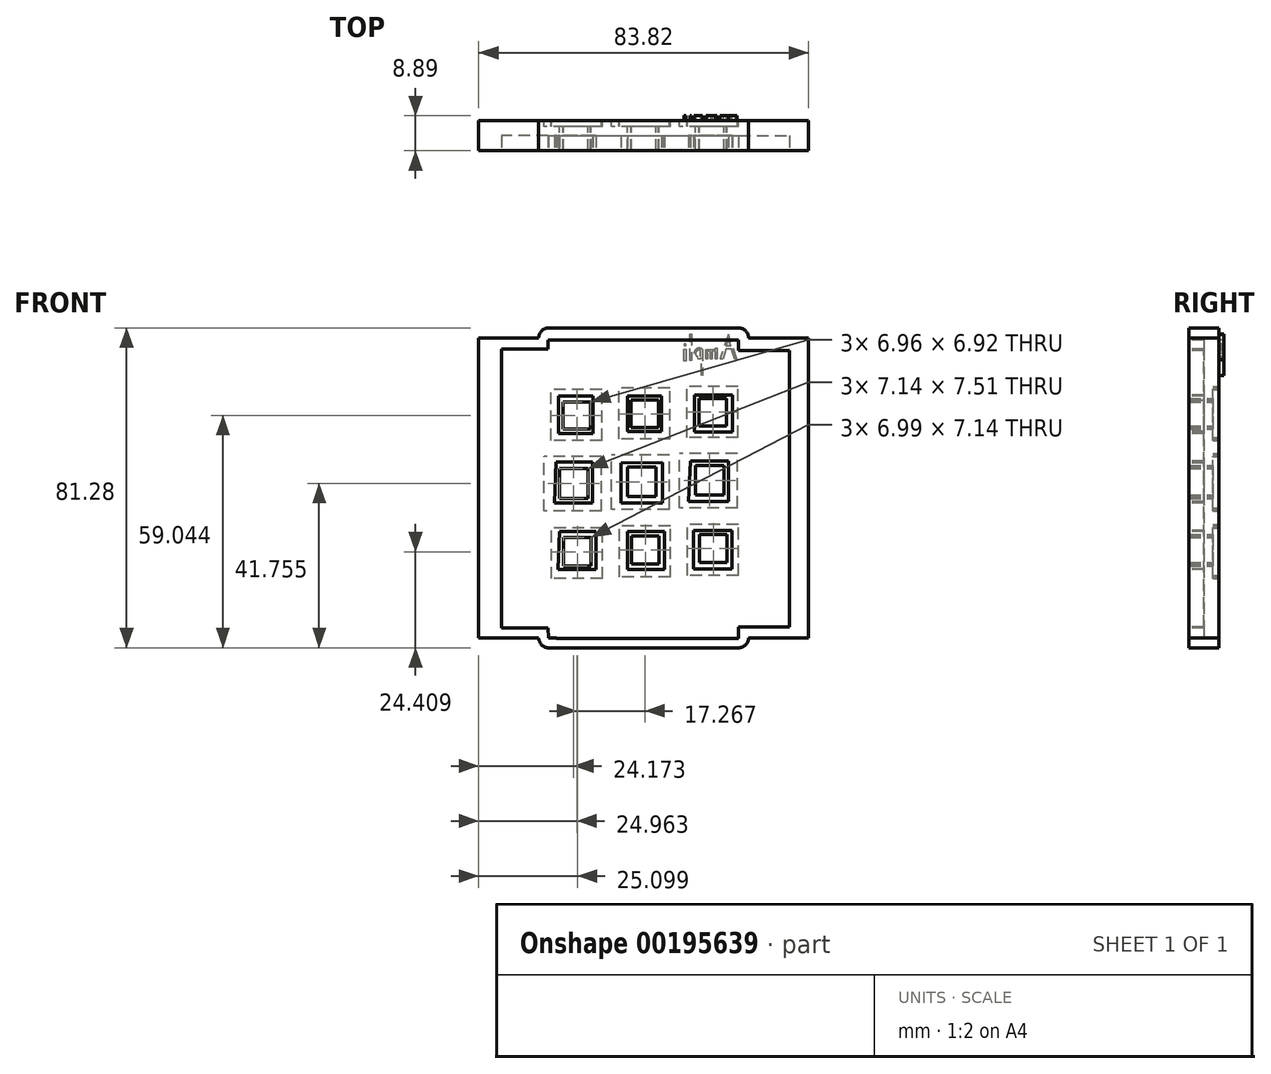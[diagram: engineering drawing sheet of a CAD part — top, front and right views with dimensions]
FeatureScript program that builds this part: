
annotation { "Feature Type Name" : "Feature", "Feature Type Description" : "" }
export const myFeature = defineFeature(function(context is Context, id is Id, definition is map)
    precondition{}
    {
        {
            var Q0;
            Q0=qCreatedBy(makeId("Front.planeOp"),FACE);
            var sketch = newSketch(context, id + "F0", { "sketchPlane" : qUnion([Q0])});
            skLineSegment(sketch, "E0.bottom", {"start": v(26.67, 27.94) * mm, "end": v(-26.67, 27.94) * mm});
            skLineSegment(sketch, "E0.top", {"start": v(26.67, -27.94) * mm, "end": v(-26.67, -27.94) * mm});
            skLineSegment(sketch, "E0.left", {"start": v(26.67, 27.94) * mm, "end": v(26.67, -27.94) * mm});
            skLineSegment(sketch, "E0.right", {"start": v(-26.67, 27.94) * mm, "end": v(-26.67, -27.94) * mm});
            skPoint(sketch, "E0.middle", {"position": v(0, 0) * mm});
            skSolve(sketch);
        }
        {
            var Q0;
            Q0 = qSketchRegion(id + "F0", true);
            extrude(context, id + "F1", {"entities" : qUnion([Q0]), "depth" : 7.62 * mm});
        }
        {
            var Q0;
            Q0=makeQuery(id+"F1.opExtrude","CAP_FACE",FACE,{"disambiguationData":[OSD([sQuery(id+"F0.wireOp",EDGE,"E0.bottom"),sQuery(id+"F0.wireOp",EDGE,"E0.top"),sQuery(id+"F0.wireOp",EDGE,"E0.left"),sQuery(id+"F0.wireOp",EDGE,"E0.right")])],"isStart":true});
            var sketch = newSketch(context, id + "F2", { "sketchPlane" : qUnion([Q0])});
            skLineSegment(sketch, "E1.bottom", {"start": v(-21.07, 22.68) * mm, "end": v(-14.1, 22.68) * mm});
            skLineSegment(sketch, "E1.top", {"start": v(-21.07, 15.76) * mm, "end": v(-14.1, 15.76) * mm});
            skLineSegment(sketch, "E1.left", {"start": v(-21.07, 22.68) * mm, "end": v(-21.07, 15.76) * mm});
            skLineSegment(sketch, "E1.right", {"start": v(-14.1, 22.68) * mm, "end": v(-14.1, 15.76) * mm});
            skLineSegment(sketch, "E2.bottom", {"start": v(-23.93, 12.85) * mm, "end": v(-11, 12.85) * mm});
            skLineSegment(sketch, "E2.top", {"start": v(-23.93, 25.79) * mm, "end": v(-11, 25.79) * mm});
            skLineSegment(sketch, "E2.left", {"start": v(-23.93, 12.85) * mm, "end": v(-23.93, 25.79) * mm});
            skLineSegment(sketch, "E2.right", {"start": v(-11, 12.85) * mm, "end": v(-11, 25.79) * mm});
            skLineSegment(sketch, "E3.1.0.0", {"start": v(3.16, 22.27) * mm, "end": v(3.16, 15.35) * mm});
            skLineSegment(sketch, "E3.1.0.1", {"start": v(-3.8, 15.35) * mm, "end": v(3.16, 15.35) * mm});
            skLineSegment(sketch, "E3.1.0.2", {"start": v(-3.8, 22.27) * mm, "end": v(-3.8, 15.35) * mm});
            skLineSegment(sketch, "E3.1.0.3", {"start": v(-3.8, 22.27) * mm, "end": v(3.16, 22.27) * mm});
            skLineSegment(sketch, "E3.1.0.4", {"start": v(6.27, 12.45) * mm, "end": v(6.27, 25.38) * mm});
            skLineSegment(sketch, "E3.1.0.5", {"start": v(-6.66, 12.45) * mm, "end": v(-6.66, 25.38) * mm});
            skLineSegment(sketch, "E3.1.0.6", {"start": v(-6.66, 12.45) * mm, "end": v(6.27, 12.45) * mm});
            skLineSegment(sketch, "E3.1.0.7", {"start": v(-6.66, 25.38) * mm, "end": v(6.27, 25.38) * mm});
            skLineSegment(sketch, "E3.2.0.0", {"start": v(20.43, 21.86) * mm, "end": v(20.43, 14.95) * mm});
            skLineSegment(sketch, "E3.2.0.1", {"start": v(13.46, 14.95) * mm, "end": v(20.43, 14.95) * mm});
            skLineSegment(sketch, "E3.2.0.2", {"start": v(13.46, 21.86) * mm, "end": v(13.46, 14.95) * mm});
            skLineSegment(sketch, "E3.2.0.3", {"start": v(13.46, 21.86) * mm, "end": v(20.43, 21.86) * mm});
            skLineSegment(sketch, "E3.2.0.4", {"start": v(23.54, 12.04) * mm, "end": v(23.54, 24.97) * mm});
            skLineSegment(sketch, "E3.2.0.5", {"start": v(10.6, 12.04) * mm, "end": v(10.6, 24.97) * mm});
            skLineSegment(sketch, "E3.2.0.6", {"start": v(10.6, 12.04) * mm, "end": v(23.54, 12.04) * mm});
            skLineSegment(sketch, "E3.2.0.7", {"start": v(10.6, 24.97) * mm, "end": v(23.54, 24.97) * mm});
            skLineSegment(sketch, "E3.direction1", {"start": v(-23.93, 12.85) * mm, "end": v(-6.66, 12.45) * mm, "construction": true});
            skPoint(sketch, "E4", {"position": v(0, 0) * mm});
            skPoint(sketch, "E5", {"position": v(-0.84, 0.87) * mm});
            skPoint(sketch, "E6", {"position": v(-0.84, -16.23) * mm});
            skLineSegment(sketch, "E7.bottom", {"start": v(-20.37, 5.69) * mm, "end": v(-13.23, 5.69) * mm});
            skLineSegment(sketch, "E7.top", {"start": v(-20.37, -1.83) * mm, "end": v(-13.23, -1.83) * mm});
            skLineSegment(sketch, "E7.left", {"start": v(-20.37, 5.69) * mm, "end": v(-20.37, -1.83) * mm});
            skLineSegment(sketch, "E7.right", {"start": v(-13.23, 5.69) * mm, "end": v(-13.23, -1.83) * mm});
            skLineSegment(sketch, "E8.bottom", {"start": v(-23.8, -5.1) * mm, "end": v(-9.18, -5.1) * mm});
            skLineSegment(sketch, "E8.top", {"start": v(-23.8, 8.75) * mm, "end": v(-9.18, 8.75) * mm});
            skLineSegment(sketch, "E8.left", {"start": v(-23.8, -5.1) * mm, "end": v(-23.8, 8.75) * mm});
            skLineSegment(sketch, "E8.right", {"start": v(-9.18, -5.1) * mm, "end": v(-9.18, 8.75) * mm});
            skLineSegment(sketch, "E9.1.0.0", {"start": v(4.04, 5.28) * mm, "end": v(4.04, -2.23) * mm});
            skLineSegment(sketch, "E9.1.0.1", {"start": v(-3.1, -2.23) * mm, "end": v(4.04, -2.23) * mm});
            skLineSegment(sketch, "E9.1.0.2", {"start": v(-3.1, 5.28) * mm, "end": v(-3.1, -2.23) * mm});
            skLineSegment(sketch, "E9.1.0.3", {"start": v(-3.1, 5.28) * mm, "end": v(4.04, 5.28) * mm});
            skLineSegment(sketch, "E9.1.0.4", {"start": v(8.09, -5.5) * mm, "end": v(8.09, 8.34) * mm});
            skLineSegment(sketch, "E9.1.0.5", {"start": v(-6.54, -5.5) * mm, "end": v(-6.54, 8.34) * mm});
            skLineSegment(sketch, "E9.1.0.6", {"start": v(-6.54, -5.5) * mm, "end": v(8.09, -5.5) * mm});
            skLineSegment(sketch, "E9.1.0.7", {"start": v(-6.54, 8.34) * mm, "end": v(8.09, 8.34) * mm});
            skLineSegment(sketch, "E9.2.0.0", {"start": v(21.3, 4.87) * mm, "end": v(21.3, -2.64) * mm});
            skLineSegment(sketch, "E9.2.0.1", {"start": v(14.17, -2.64) * mm, "end": v(21.3, -2.64) * mm});
            skLineSegment(sketch, "E9.2.0.2", {"start": v(14.17, 4.87) * mm, "end": v(14.17, -2.64) * mm});
            skLineSegment(sketch, "E9.2.0.3", {"start": v(14.17, 4.87) * mm, "end": v(21.3, 4.87) * mm});
            skLineSegment(sketch, "E9.2.0.4", {"start": v(25.36, -5.91) * mm, "end": v(25.36, 7.93) * mm});
            skLineSegment(sketch, "E9.2.0.5", {"start": v(10.73, -5.91) * mm, "end": v(10.73, 7.93) * mm});
            skLineSegment(sketch, "E9.2.0.6", {"start": v(10.73, -5.91) * mm, "end": v(25.36, -5.91) * mm});
            skLineSegment(sketch, "E9.2.0.7", {"start": v(10.73, 7.93) * mm, "end": v(25.36, 7.93) * mm});
            skLineSegment(sketch, "E9.direction1", {"start": v(-23.8, -5.1) * mm, "end": v(-6.54, -5.5) * mm, "construction": true});
            skLineSegment(sketch, "E10.bottom", {"start": v(-21.22, -11.85) * mm, "end": v(-14.23, -11.85) * mm});
            skLineSegment(sketch, "E10.top", {"start": v(-21.22, -18.99) * mm, "end": v(-14.23, -18.99) * mm});
            skLineSegment(sketch, "E10.left", {"start": v(-21.22, -11.85) * mm, "end": v(-21.22, -18.99) * mm});
            skLineSegment(sketch, "E10.right", {"start": v(-14.23, -11.85) * mm, "end": v(-14.23, -18.99) * mm});
            skLineSegment(sketch, "E11.bottom", {"start": v(-24.05, -22.26) * mm, "end": v(-11.12, -22.26) * mm});
            skLineSegment(sketch, "E11.top", {"start": v(-24.05, -9.33) * mm, "end": v(-11.12, -9.33) * mm});
            skLineSegment(sketch, "E11.left", {"start": v(-24.05, -22.26) * mm, "end": v(-24.05, -9.33) * mm});
            skLineSegment(sketch, "E11.right", {"start": v(-11.12, -22.26) * mm, "end": v(-11.12, -9.33) * mm});
            skLineSegment(sketch, "E12.1.0.0", {"start": v(3.04, -12.25) * mm, "end": v(3.04, -19.4) * mm});
            skLineSegment(sketch, "E12.1.0.1", {"start": v(-3.95, -19.4) * mm, "end": v(3.04, -19.4) * mm});
            skLineSegment(sketch, "E12.1.0.2", {"start": v(-3.95, -12.25) * mm, "end": v(-3.95, -19.4) * mm});
            skLineSegment(sketch, "E12.1.0.3", {"start": v(-3.95, -12.25) * mm, "end": v(3.04, -12.25) * mm});
            skLineSegment(sketch, "E12.1.0.4", {"start": v(6.15, -22.67) * mm, "end": v(6.15, -9.74) * mm});
            skLineSegment(sketch, "E12.1.0.5", {"start": v(-6.78, -22.67) * mm, "end": v(-6.78, -9.74) * mm});
            skLineSegment(sketch, "E12.1.0.6", {"start": v(-6.78, -22.67) * mm, "end": v(6.15, -22.67) * mm});
            skLineSegment(sketch, "E12.1.0.7", {"start": v(-6.78, -9.74) * mm, "end": v(6.15, -9.74) * mm});
            skLineSegment(sketch, "E12.2.0.0", {"start": v(20.3, -12.66) * mm, "end": v(20.3, -19.8) * mm});
            skLineSegment(sketch, "E12.2.0.1", {"start": v(13.32, -19.8) * mm, "end": v(20.3, -19.8) * mm});
            skLineSegment(sketch, "E12.2.0.2", {"start": v(13.32, -12.66) * mm, "end": v(13.32, -19.8) * mm});
            skLineSegment(sketch, "E12.2.0.3", {"start": v(13.32, -12.66) * mm, "end": v(20.3, -12.66) * mm});
            skLineSegment(sketch, "E12.2.0.4", {"start": v(23.42, -23.08) * mm, "end": v(23.42, -10.14) * mm});
            skLineSegment(sketch, "E12.2.0.5", {"start": v(10.48, -23.08) * mm, "end": v(10.48, -10.14) * mm});
            skLineSegment(sketch, "E12.2.0.6", {"start": v(10.48, -23.08) * mm, "end": v(23.42, -23.08) * mm});
            skLineSegment(sketch, "E12.2.0.7", {"start": v(10.48, -10.14) * mm, "end": v(23.42, -10.14) * mm});
            skLineSegment(sketch, "E12.direction1", {"start": v(-24.05, -22.26) * mm, "end": v(-6.78, -22.67) * mm, "construction": true});
            skSolve(sketch);
        }
        {
            var Q0;
            Q0=makeQuery(id+"F2.imprint","IMPRINT",FACE,{"disambiguationData":[TD([[makeQuery(id+"F2.imprint","IMPRINT",EDGE,{"derivedFrom":sQuery(id+"F2.wireOp",EDGE,"E1.bottom")}),-1.0]])]});
            var Q1;
            Q1=makeQuery(id+"F2.imprint","IMPRINT",FACE,{"disambiguationData":[TD([[makeQuery(id+"F2.imprint","IMPRINT",EDGE,{"derivedFrom":sQuery(id+"F2.wireOp",EDGE,"E3.1.0.0")}),-1.0]])]});
            var Q2;
            Q2=makeQuery(id+"F2.imprint","IMPRINT",FACE,{"disambiguationData":[TD([[makeQuery(id+"F2.imprint","IMPRINT",EDGE,{"derivedFrom":sQuery(id+"F2.wireOp",EDGE,"E9.2.0.0")}),-1.0]])]});
            var Q3;
            Q3=makeQuery(id+"F2.imprint","IMPRINT",FACE,{"disambiguationData":[TD([[makeQuery(id+"F2.imprint","IMPRINT",EDGE,{"derivedFrom":sQuery(id+"F2.wireOp",EDGE,"E3.2.0.0")}),-1.0]])]});
            var Q4;
            Q4=makeQuery(id+"F2.imprint","IMPRINT",FACE,{"disambiguationData":[TD([[makeQuery(id+"F2.imprint","IMPRINT",EDGE,{"derivedFrom":sQuery(id+"F2.wireOp",EDGE,"E9.1.0.0")}),-1.0]])]});
            var Q5;
            Q5=makeQuery(id+"F2.imprint","IMPRINT",FACE,{"disambiguationData":[TD([[makeQuery(id+"F2.imprint","IMPRINT",EDGE,{"derivedFrom":sQuery(id+"F2.wireOp",EDGE,"E7.bottom")}),-1.0]])]});
            var Q6;
            Q6=makeQuery(id+"F2.imprint","IMPRINT",FACE,{"disambiguationData":[TD([[makeQuery(id+"F2.imprint","IMPRINT",EDGE,{"derivedFrom":sQuery(id+"F2.wireOp",EDGE,"E10.bottom")}),-1.0]])]});
            var Q7;
            Q7=makeQuery(id+"F2.imprint","IMPRINT",FACE,{"disambiguationData":[TD([[makeQuery(id+"F2.imprint","IMPRINT",EDGE,{"derivedFrom":sQuery(id+"F2.wireOp",EDGE,"E12.1.0.0")}),-1.0]])]});
            var Q8;
            Q8=makeQuery(id+"F2.imprint","IMPRINT",FACE,{"disambiguationData":[TD([[makeQuery(id+"F2.imprint","IMPRINT",EDGE,{"derivedFrom":sQuery(id+"F2.wireOp",EDGE,"E12.2.0.0")}),-1.0]])]});
            extrude(context, id + "F3", {"entities" : qUnion([Q0, Q1, Q2, Q3, Q4, Q5, Q6, Q7, Q8]), "operationType" : NewBodyOperationType.REMOVE, "oppositeDirection" : true, "depth" : 12.7 * mm});
        }
        {
            var Q0;
            Q0 = qSketchRegion(id + "F2", true);
            var Q1;
            Q1=makeQuery(id+"F1.opExtrude","CAP_FACE",FACE,{"disambiguationData":[OSD([sQuery(id+"F0.wireOp",EDGE,"E0.bottom"),sQuery(id+"F0.wireOp",EDGE,"E0.top"),sQuery(id+"F0.wireOp",EDGE,"E0.left"),sQuery(id+"F0.wireOp",EDGE,"E0.right")])],"isStart":false});
            extrude(context, id + "F4", {"entities" : qUnion([Q0, Q1]), "operationType" : NewBodyOperationType.REMOVE, "oppositeDirection" : true, "depth" : 1.52 * mm});
        }
        {
            var Q0;
            Q0=makeQuery(id+"F1.opExtrude","SWEPT_FACE",FACE,{"disambiguationData":[OSD([sQuery(id+"F0.wireOp",EDGE,"E0.top")])]});
            extrude(context, id + "F5", {"entities" : qUnion([Q0]), "operationType" : NewBodyOperationType.ADD, "depth" : 12.7 * mm});
        }
        {
            var Q0;
            Q0=makeQuery(id+"F1.opExtrude","SWEPT_FACE",FACE,{"disambiguationData":[OSD([sQuery(id+"F0.wireOp",EDGE,"E0.bottom")])]});
            extrude(context, id + "F6", {"entities" : qUnion([Q0]), "operationType" : NewBodyOperationType.ADD, "depth" : 12.7 * mm});
        }
        {
            var Q0;
            {var subQ0=sQuery(id+"F0.wireOp",EDGE,"E0.bottom");var subQ1=sQuery(id+"F0.wireOp",EDGE,"E0.top");Q0=makeQuery(id+"F6.boolean.opBoolean","MERGE",FACE,{"derivedFrom":[makeQuery(id+"F5.boolean.opBoolean","MERGE",FACE,{"derivedFrom":[makeQuery(id+"F1.opExtrude","CAP_FACE",FACE,{"disambiguationData":[OSD([subQ0,subQ1,sQuery(id+"F0.wireOp",EDGE,"E0.left"),sQuery(id+"F0.wireOp",EDGE,"E0.right")])],"isStart":false}),makeQuery(id+"F5.opExtrude","SWEPT_FACE",FACE,{"disambiguationData":[OSD([subQ1]),TDD([makeQuery(id+"F1.opExtrude","CAP_EDGE",EDGE,{"disambiguationData":[OSD([subQ1])],"isStart":false})])]})]}),makeQuery(id+"F6.opExtrude","SWEPT_FACE",FACE,{"disambiguationData":[OSD([subQ0]),TDD([makeQuery(id+"F1.opExtrude","CAP_EDGE",EDGE,{"disambiguationData":[OSD([subQ0])],"isStart":false})])]})]});}
            var sketch = newSketch(context, id + "F7", { "sketchPlane" : qUnion([Q0])});
            skLineSegment(sketch, "E13.bottom", {"start": v(-24.22, 37.51) * mm, "end": v(24.15, 37.51) * mm});
            skLineSegment(sketch, "E13.top", {"start": v(-24.22, 28.3) * mm, "end": v(24.15, 28.3) * mm});
            skLineSegment(sketch, "E13.left", {"start": v(-24.22, 37.51) * mm, "end": v(-24.22, 28.3) * mm});
            skLineSegment(sketch, "E13.right", {"start": v(24.15, 37.51) * mm, "end": v(24.15, 28.3) * mm});
            skLineSegment(sketch, "E14.bottom", {"start": v(-22.08, -29.11) * mm, "end": v(24.15, -29.11) * mm});
            skLineSegment(sketch, "E14.top", {"start": v(-22.08, -38.32) * mm, "end": v(24.15, -38.32) * mm});
            skLineSegment(sketch, "E14.left", {"start": v(-22.08, -29.11) * mm, "end": v(-22.08, -38.32) * mm});
            skLineSegment(sketch, "E14.right", {"start": v(24.15, -29.11) * mm, "end": v(24.15, -38.32) * mm});
            skSolve(sketch);
        }
        {
            var Q0;
            Q0=makeQuery(id+"F7.imprint","IMPRINT",FACE,{"disambiguationData":[TD([[makeQuery(id+"F7.imprint","IMPRINT",EDGE,{"derivedFrom":sQuery(id+"F7.wireOp",EDGE,"E13.bottom")}),-1.0]])]});
            var Q1;
            Q1=makeQuery(id+"F7.imprint","IMPRINT",FACE,{"disambiguationData":[TD([[makeQuery(id+"F7.imprint","IMPRINT",EDGE,{"derivedFrom":sQuery(id+"F7.wireOp",EDGE,"E14.bottom")}),-1.0]])]});
            extrude(context, id + "F8", {"entities" : qUnion([Q0, Q1]), "operationType" : NewBodyOperationType.REMOVE, "oppositeDirection" : true, "depth" : 3.8 * mm});
        }
        {
            var Q0;
            {var subQ0=sQuery(id+"F0.wireOp",EDGE,"E0.bottom");var subQ1=sQuery(id+"F0.wireOp",EDGE,"E0.top");Q0=makeQuery(id+"F6.boolean.opBoolean","MERGE",FACE,{"derivedFrom":[makeQuery(id+"F5.boolean.opBoolean","MERGE",FACE,{"derivedFrom":[makeQuery(id+"F1.opExtrude","CAP_FACE",FACE,{"disambiguationData":[OSD([subQ0,subQ1,sQuery(id+"F0.wireOp",EDGE,"E0.left"),sQuery(id+"F0.wireOp",EDGE,"E0.right")])],"isStart":true}),makeQuery(id+"F5.opExtrude","SWEPT_FACE",FACE,{"disambiguationData":[OSD([subQ1]),TDD([makeQuery(id+"F1.opExtrude","CAP_EDGE",EDGE,{"disambiguationData":[OSD([subQ1])],"isStart":true})])]})]}),makeQuery(id+"F6.opExtrude","SWEPT_FACE",FACE,{"disambiguationData":[OSD([subQ0]),TDD([makeQuery(id+"F1.opExtrude","CAP_EDGE",EDGE,{"disambiguationData":[OSD([subQ0])],"isStart":true})])]})]});}
            var sketch = newSketch(context, id + "F9", { "sketchPlane" : qUnion([Q0])});
            skLineSegment(sketch, "E15", {"start": v(-23.76, 32.62) * mm, "end": v(-21.56, 39) * mm});
            skLineSegment(sketch, "E16", {"start": v(-21.56, 39) * mm, "end": v(-19.44, 32.76) * mm});
            skLineSegment(sketch, "E17", {"start": v(-23.76, 32.62) * mm, "end": v(-23.22, 32.62) * mm});
            skLineSegment(sketch, "E18", {"start": v(-23.22, 32.62) * mm, "end": v(-22.29, 35.33) * mm});
            skLineSegment(sketch, "E19", {"start": v(-22.29, 35.33) * mm, "end": v(-20.93, 35.33) * mm});
            skLineSegment(sketch, "E20", {"start": v(-20.93, 35.33) * mm, "end": v(-20.14, 32.76) * mm});
            skLineSegment(sketch, "E21", {"start": v(-20.14, 32.76) * mm, "end": v(-19.44, 32.76) * mm});
            skLineSegment(sketch, "E22", {"start": v(-21.55, 37.56) * mm, "end": v(-22.07, 36.06) * mm});
            skLineSegment(sketch, "E23", {"start": v(-22.07, 36.06) * mm, "end": v(-20.93, 36.06) * mm});
            skLineSegment(sketch, "E24", {"start": v(-20.93, 36.06) * mm, "end": v(-21.55, 37.56) * mm});
            skLineSegment(sketch, "E25", {"start": v(-18.6, 32.76) * mm, "end": v(-18.29, 32.76) * mm});
            skLineSegment(sketch, "E26", {"start": v(-18.29, 32.76) * mm, "end": v(-18.29, 34.36) * mm});
            skArc(sketch, "E27", {"start": v(-18.29, 34.36) * mm, "mid": v(-17.83, 34.81) * mm, "end": v(-17.38, 34.36) * mm});
            skLineSegment(sketch, "E28", {"start": v(-17.38, 34.36) * mm, "end": v(-17.38, 32.79) * mm});
            skLineSegment(sketch, "E29", {"start": v(-17.38, 32.79) * mm, "end": v(-17.06, 32.79) * mm});
            skLineSegment(sketch, "E30", {"start": v(-17.06, 32.79) * mm, "end": v(-17.06, 34.36) * mm});
            skArc(sketch, "E31", {"start": v(-17.06, 34.36) * mm, "mid": v(-16.5, 34.8) * mm, "end": v(-16.18, 34.17) * mm});
            skLineSegment(sketch, "E32", {"start": v(-16.18, 34.17) * mm, "end": v(-16.18, 32.73) * mm});
            skLineSegment(sketch, "E33", {"start": v(-16.18, 32.73) * mm, "end": v(-15.87, 32.73) * mm});
            skLineSegment(sketch, "E34", {"start": v(-15.87, 32.73) * mm, "end": v(-15.87, 35.18) * mm});
            skLineSegment(sketch, "E35", {"start": v(-15.87, 35.18) * mm, "end": v(-18.22, 35.18) * mm});
            skLineSegment(sketch, "E36", {"start": v(-18.22, 35.18) * mm, "end": v(-18.22, 35.55) * mm});
            skLineSegment(sketch, "E37", {"start": v(-18.22, 35.55) * mm, "end": v(-18.6, 35.55) * mm});
            skLineSegment(sketch, "E38", {"start": v(-18.6, 35.55) * mm, "end": v(-18.6, 32.76) * mm});
            skLineSegment(sketch, "E39", {"start": v(-14.98, 35.18) * mm, "end": v(-14.98, 28.55) * mm});
            skLineSegment(sketch, "E40", {"start": v(-14.98, 28.55) * mm, "end": v(-14.71, 28.64) * mm});
            skLineSegment(sketch, "E41", {"start": v(-14.71, 28.64) * mm, "end": v(-14.71, 32.98) * mm});
            skArc(sketch, "E42", {"start": v(-14.71, 32.98) * mm, "mid": v(-12.83, 34.32) * mm, "end": v(-14.98, 35.18) * mm});
            skLineSegment(sketch, "E43", {"start": v(-14.5, 33.32) * mm, "end": v(-14.5, 34.92) * mm});
            skArc(sketch, "E44", {"start": v(-14.5, 33.32) * mm, "mid": v(-13.2, 34.12) * mm, "end": v(-14.5, 34.92) * mm});
            skLineSegment(sketch, "E45", {"start": v(-12.14, 39.1) * mm, "end": v(-12.14, 32.41) * mm});
            skLineSegment(sketch, "E46", {"start": v(-12.14, 32.41) * mm, "end": v(-11.8, 32.41) * mm});
            skLineSegment(sketch, "E47", {"start": v(-11.8, 32.41) * mm, "end": v(-11.8, 39.07) * mm});
            skLineSegment(sketch, "E48", {"start": v(-11.8, 39.07) * mm, "end": v(-12.14, 39.1) * mm});
            skLineSegment(sketch, "E49", {"start": v(-10.72, 35.27) * mm, "end": v(-10.72, 32.29) * mm});
            skLineSegment(sketch, "E50", {"start": v(-10.72, 32.29) * mm, "end": v(-10.31, 32.29) * mm});
            skLineSegment(sketch, "E51", {"start": v(-10.31, 32.29) * mm, "end": v(-10.31, 35.24) * mm});
            skLineSegment(sketch, "E52", {"start": v(-10.31, 35.24) * mm, "end": v(-10.66, 35.2) * mm});
            skLineSegment(sketch, "E53", {"start": v(-10.66, 35.2) * mm, "end": v(-10.72, 35.27) * mm});
            skPoint(sketch, "E54", {"position": v(-10.53, 36.34) * mm});
            skCircle(sketch, "E55", {"center": v(-10.53, 36.34) * mm, "radius": 0.22 * mm});
            skSolve(sketch);
        }
        {
            var Q0;
            Q0=makeQuery(id+"F9.imprint","IMPRINT",FACE,{"disambiguationData":[TD([[makeQuery(id+"F9.imprint","IMPRINT",EDGE,{"derivedFrom":sQuery(id+"F9.wireOp",EDGE,"E15")}),-1.0]])]});
            var Q1;
            Q1=makeQuery(id+"F9.imprint","IMPRINT",FACE,{"disambiguationData":[TD([[makeQuery(id+"F9.imprint","IMPRINT",EDGE,{"derivedFrom":sQuery(id+"F9.wireOp",EDGE,"E25")}),1.0]])]});
            var Q2;
            Q2=makeQuery(id+"F9.imprint","IMPRINT",FACE,{"disambiguationData":[TD([[makeQuery(id+"F9.imprint","IMPRINT",EDGE,{"derivedFrom":sQuery(id+"F9.wireOp",EDGE,"E39")}),1.0]])]});
            var Q3;
            Q3=makeQuery(id+"F9.imprint","IMPRINT",FACE,{"disambiguationData":[TD([[makeQuery(id+"F9.imprint","IMPRINT",EDGE,{"derivedFrom":sQuery(id+"F9.wireOp",EDGE,"E45")}),1.0]])]});
            var Q4;
            Q4=makeQuery(id+"F9.imprint","IMPRINT",FACE,{"disambiguationData":[TD([[makeQuery(id+"F9.imprint","IMPRINT",EDGE,{"derivedFrom":sQuery(id+"F9.wireOp",EDGE,"E49")}),1.0]])]});
            var Q5;
            Q5=makeQuery(id+"F9.imprint","IMPRINT",FACE,{"disambiguationData":[TD([[makeQuery(id+"F9.imprint","IMPRINT",EDGE,{"derivedFrom":sQuery(id+"F9.wireOp",EDGE,"E55")}),1.0]])]});
            extrude(context, id + "F10", {"entities" : qUnion([Q0, Q1, Q2, Q3, Q4, Q5]), "operationType" : NewBodyOperationType.ADD, "depth" : 1.27 * mm});
        }
        {
            var Q0;
            Q0=makeQuery(id+"F5.opExtrude","CAP_EDGE",EDGE,{"disambiguationData":[OSD([sQuery(id+"F0.wireOp",EDGE,"E0.top"),sQuery(id+"F0.wireOp",EDGE,"E0.right")])],"isStart":false});
            var Q1;
            Q1=makeQuery(id+"F5.opExtrude","CAP_EDGE",EDGE,{"disambiguationData":[OSD([sQuery(id+"F0.wireOp",EDGE,"E0.top"),sQuery(id+"F0.wireOp",EDGE,"E0.left")])],"isStart":false});
            var Q2;
            Q2=makeQuery(id+"F6.opExtrude","CAP_EDGE",EDGE,{"disambiguationData":[OSD([sQuery(id+"F0.wireOp",EDGE,"E0.bottom"),sQuery(id+"F0.wireOp",EDGE,"E0.right")])],"isStart":false});
            var Q3;
            Q3=makeQuery(id+"F6.opExtrude","CAP_EDGE",EDGE,{"disambiguationData":[OSD([sQuery(id+"F0.wireOp",EDGE,"E0.bottom"),sQuery(id+"F0.wireOp",EDGE,"E0.left")])],"isStart":false});
            fillet(context, id + "F11", {"entities" : qUnion([Q0, Q1, Q2, Q3]), "radius" : 2.54 * mm, "tangentPropagation" : true, "allowEdgeOverflow" : false});
        }
        {
            var Q0;
            {var subQ0=sQuery(id+"F0.wireOp",EDGE,"E0.left");Q0=makeQuery(id+"F6.boolean.opBoolean","MERGE",FACE,{"derivedFrom":[makeQuery(id+"F5.boolean.opBoolean","MERGE",FACE,{"derivedFrom":[makeQuery(id+"F1.opExtrude","SWEPT_FACE",FACE,{"disambiguationData":[OSD([subQ0])]}),makeQuery(id+"F5.opExtrude","SWEPT_FACE",FACE,{"disambiguationData":[OSD([sQuery(id+"F0.wireOp",EDGE,"E0.top"),subQ0])]})]}),makeQuery(id+"F6.opExtrude","SWEPT_FACE",FACE,{"disambiguationData":[OSD([sQuery(id+"F0.wireOp",EDGE,"E0.bottom"),subQ0])]})]});}
            extrude(context, id + "F12", {"entities" : qUnion([Q0]), "operationType" : NewBodyOperationType.ADD, "depth" : 25.4 * mm});
        }
        {
            var Q0;
            {var subQ0=sQuery(id+"F0.wireOp",EDGE,"E0.right");Q0=makeQuery(id+"F6.boolean.opBoolean","MERGE",FACE,{"derivedFrom":[makeQuery(id+"F5.boolean.opBoolean","MERGE",FACE,{"derivedFrom":[makeQuery(id+"F1.opExtrude","SWEPT_FACE",FACE,{"disambiguationData":[OSD([subQ0])]}),makeQuery(id+"F5.opExtrude","SWEPT_FACE",FACE,{"disambiguationData":[OSD([sQuery(id+"F0.wireOp",EDGE,"E0.top"),subQ0])]})]}),makeQuery(id+"F6.opExtrude","SWEPT_FACE",FACE,{"disambiguationData":[OSD([sQuery(id+"F0.wireOp",EDGE,"E0.bottom"),subQ0])]})]});}
            extrude(context, id + "F13", {"entities" : qUnion([Q0]), "operationType" : NewBodyOperationType.ADD, "depth" : 25.4 * mm});
        }
        {
            var Q0;
            {var subQ0=sQuery(id+"F0.wireOp",EDGE,"E0.right");var subQ1=sQuery(id+"F0.wireOp",EDGE,"E0.bottom");var subQ2=sQuery(id+"F0.wireOp",EDGE,"E0.top");var subQ3=sQuery(id+"F0.wireOp",EDGE,"E0.left");Q0=makeQuery(id+"F13.boolean.opBoolean","MERGE",FACE,{"derivedFrom":[makeQuery(id+"F12.boolean.opBoolean","MERGE",FACE,{"derivedFrom":[makeQuery(id+"F6.boolean.opBoolean","MERGE",FACE,{"derivedFrom":[makeQuery(id+"F5.boolean.opBoolean","MERGE",FACE,{"derivedFrom":[makeQuery(id+"F1.opExtrude","CAP_FACE",FACE,{"disambiguationData":[OSD([subQ1,subQ2,subQ3,subQ0])],"isStart":false}),makeQuery(id+"F5.opExtrude","SWEPT_FACE",FACE,{"disambiguationData":[OSD([subQ2]),TDD([makeQuery(id+"F1.opExtrude","CAP_EDGE",EDGE,{"disambiguationData":[OSD([subQ2])],"isStart":false})])]})]}),makeQuery(id+"F6.opExtrude","SWEPT_FACE",FACE,{"disambiguationData":[OSD([subQ1]),TDD([makeQuery(id+"F1.opExtrude","CAP_EDGE",EDGE,{"disambiguationData":[OSD([subQ1])],"isStart":false})])]})]}),makeQuery(id+"F12.opExtrude","SWEPT_FACE",FACE,{"disambiguationData":[OSD([subQ1,subQ2,subQ3]),TDD([makeQuery(id+"F6.boolean.opBoolean","MERGE",EDGE,{"derivedFrom":[makeQuery(id+"F5.boolean.opBoolean","MERGE",EDGE,{"derivedFrom":[makeQuery(id+"F1.opExtrude","CAP_EDGE",EDGE,{"disambiguationData":[OSD([subQ3])],"isStart":false}),makeQuery(id+"F5.opExtrude","SWEPT_EDGE",EDGE,{"disambiguationData":[OSD([subQ2,subQ3]),TDD([makeQuery(id+"F1.opExtrude","CAP_VERTEX",VERTEX,{"disambiguationData":[OSD([subQ2,subQ3])],"isStart":false})])]})]}),makeQuery(id+"F6.opExtrude","SWEPT_EDGE",EDGE,{"disambiguationData":[OSD([subQ1,subQ3]),TDD([makeQuery(id+"F1.opExtrude","CAP_VERTEX",VERTEX,{"disambiguationData":[OSD([subQ1,subQ3])],"isStart":false})])]})]})])]})]}),makeQuery(id+"F13.opExtrude","SWEPT_FACE",FACE,{"disambiguationData":[OSD([subQ1,subQ2,subQ0]),TDD([makeQuery(id+"F6.boolean.opBoolean","MERGE",EDGE,{"derivedFrom":[makeQuery(id+"F5.boolean.opBoolean","MERGE",EDGE,{"derivedFrom":[makeQuery(id+"F1.opExtrude","CAP_EDGE",EDGE,{"disambiguationData":[OSD([subQ0])],"isStart":false}),makeQuery(id+"F5.opExtrude","SWEPT_EDGE",EDGE,{"disambiguationData":[OSD([subQ2,subQ0]),TDD([makeQuery(id+"F1.opExtrude","CAP_VERTEX",VERTEX,{"disambiguationData":[OSD([subQ2,subQ0])],"isStart":false})])]})]}),makeQuery(id+"F6.opExtrude","SWEPT_EDGE",EDGE,{"disambiguationData":[OSD([subQ1,subQ0]),TDD([makeQuery(id+"F1.opExtrude","CAP_VERTEX",VERTEX,{"disambiguationData":[OSD([subQ1,subQ0])],"isStart":false})])]})]})])]})]});}
            var sketch = newSketch(context, id + "F14", { "sketchPlane" : qUnion([Q0])});
            skLineSegment(sketch, "E56", {"start": v(-24.22, 37.51) * mm, "end": v(-24.22, 35.31) * mm});
            skLineSegment(sketch, "E57", {"start": v(-24.22, 35.31) * mm, "end": v(-36.07, 35.31) * mm});
            skLineSegment(sketch, "E58", {"start": v(-36.07, 35.31) * mm, "end": v(-36.07, -35.66) * mm});
            skLineSegment(sketch, "E59", {"start": v(-36.07, -35.66) * mm, "end": v(-24.22, -35.66) * mm});
            skLineSegment(sketch, "E60", {"start": v(-24.22, -35.66) * mm, "end": v(-24.13, -38.1) * mm});
            skLineSegment(sketch, "E61", {"start": v(-24.13, -38.1) * mm, "end": v(24.15, -38.32) * mm});
            skLineSegment(sketch, "E62", {"start": v(24.15, -35.35) * mm, "end": v(37.05, -35.35) * mm});
            skLineSegment(sketch, "E63", {"start": v(37.05, -35.35) * mm, "end": v(37.05, 34.85) * mm});
            skLineSegment(sketch, "E64", {"start": v(37.05, 34.85) * mm, "end": v(24.15, 34.85) * mm});
            skLineSegment(sketch, "E65", {"start": v(24.15, 34.85) * mm, "end": v(24.15, 37.51) * mm});
            skLineSegment(sketch, "E66", {"start": v(24.15, 37.51) * mm, "end": v(-24.22, 37.51) * mm});
            skLineSegment(sketch, "E67", {"start": v(-20.68, 23.32) * mm, "end": v(-12.8, 23.32) * mm});
            skLineSegment(sketch, "E68", {"start": v(-12.8, 23.32) * mm, "end": v(-12.8, 13.82) * mm});
            skLineSegment(sketch, "E69", {"start": v(-12.8, 13.82) * mm, "end": v(-21.65, 13.82) * mm});
            skLineSegment(sketch, "E70", {"start": v(-21.65, 13.82) * mm, "end": v(-21.65, 23.32) * mm});
            skLineSegment(sketch, "E71", {"start": v(-21.65, 23.32) * mm, "end": v(-20.68, 23.32) * mm});
            skLineSegment(sketch, "E72", {"start": v(-4.06, 23.32) * mm, "end": v(4.58, 23.32) * mm});
            skLineSegment(sketch, "E73", {"start": v(4.58, 23.32) * mm, "end": v(4.58, 14.26) * mm});
            skLineSegment(sketch, "E74", {"start": v(4.58, 14.26) * mm, "end": v(-4.06, 14.26) * mm});
            skLineSegment(sketch, "E75", {"start": v(-4.06, 23.32) * mm, "end": v(-4.06, 14.26) * mm});
            skLineSegment(sketch, "E76", {"start": v(-22.27, 6.58) * mm, "end": v(-12.94, 6.58) * mm});
            skLineSegment(sketch, "E77", {"start": v(-12.94, 6.58) * mm, "end": v(-12.94, -3.9) * mm});
            skLineSegment(sketch, "E78", {"start": v(-12.94, -3.9) * mm, "end": v(-22.63, -3.9) * mm});
            skLineSegment(sketch, "E79", {"start": v(-22.63, -3.9) * mm, "end": v(-22.27, 6.58) * mm});
            skLineSegment(sketch, "E80", {"start": v(4.8, 6.44) * mm, "end": v(4.8, -3.9) * mm});
            skLineSegment(sketch, "E81", {"start": v(4.8, -3.9) * mm, "end": v(-5.68, -3.9) * mm});
            skLineSegment(sketch, "E82", {"start": v(-5.68, -3.9) * mm, "end": v(-5.68, 6.35) * mm});
            skLineSegment(sketch, "E83", {"start": v(12.9, 22.68) * mm, "end": v(12.9, 14.14) * mm});
            skLineSegment(sketch, "E84", {"start": v(12.9, 14.14) * mm, "end": v(22.63, 14.14) * mm});
            skLineSegment(sketch, "E85", {"start": v(22.63, 14.14) * mm, "end": v(22.63, 23.56) * mm});
            skLineSegment(sketch, "E86", {"start": v(22.63, 23.56) * mm, "end": v(12.97, 23.56) * mm});
            skLineSegment(sketch, "E87", {"start": v(12.97, 23.56) * mm, "end": v(12.9, 22.24) * mm});
            skLineSegment(sketch, "E88", {"start": v(11.9, 6.86) * mm, "end": v(21.55, 6.86) * mm});
            skLineSegment(sketch, "E89", {"start": v(21.55, 6.86) * mm, "end": v(21.55, -3.46) * mm});
            skLineSegment(sketch, "E90", {"start": v(21.55, -3.46) * mm, "end": v(11.42, -3.46) * mm});
            skLineSegment(sketch, "E91", {"start": v(11.42, -3.46) * mm, "end": v(11.9, 6.86) * mm});
            skLineSegment(sketch, "E92", {"start": v(13.23, -10.8) * mm, "end": v(22.48, -10.8) * mm});
            skLineSegment(sketch, "E93", {"start": v(22.48, -10.8) * mm, "end": v(22.48, -20.33) * mm});
            skLineSegment(sketch, "E94", {"start": v(13.23, -10.8) * mm, "end": v(12.67, -10.8) * mm});
            skLineSegment(sketch, "E95", {"start": v(12.67, -10.8) * mm, "end": v(12.67, -20.65) * mm});
            skLineSegment(sketch, "E96", {"start": v(12.67, -20.65) * mm, "end": v(22.48, -20.65) * mm});
            skLineSegment(sketch, "E97", {"start": v(22.48, -20.65) * mm, "end": v(22.48, -20.33) * mm});
            skLineSegment(sketch, "E98", {"start": v(-21.42, -11.14) * mm, "end": v(-12.13, -11.14) * mm});
            skLineSegment(sketch, "E99", {"start": v(-12.13, -11.14) * mm, "end": v(-12.13, -20.69) * mm});
            skLineSegment(sketch, "E100", {"start": v(-12.13, -20.69) * mm, "end": v(-21.73, -20.69) * mm});
            skLineSegment(sketch, "E101", {"start": v(-21.73, -20.69) * mm, "end": v(-21.42, -11.14) * mm});
            skLineSegment(sketch, "E102", {"start": v(-3.51, -11.14) * mm, "end": v(5.29, -11.14) * mm});
            skLineSegment(sketch, "E103", {"start": v(5.29, -11.14) * mm, "end": v(5.29, -20.69) * mm});
            skLineSegment(sketch, "E104", {"start": v(5.29, -20.69) * mm, "end": v(-4.05, -20.69) * mm});
            skLineSegment(sketch, "E105", {"start": v(-4.05, -20.69) * mm, "end": v(-4.05, -11.14) * mm});
            skLineSegment(sketch, "E106", {"start": v(-4.05, -11.14) * mm, "end": v(-3.51, -11.14) * mm});
            skLineSegment(sketch, "E107", {"start": v(-5.68, 6.35) * mm, "end": v(4.8, 6.44) * mm});
            skSolve(sketch);
        }
        {
            var Q0;
            {var subQ7=sQuery(id+"F14.wireOp",EDGE,"E57");Q0=makeQuery(id+"F14.imprint","IMPRINT",FACE,{"disambiguationData":[TD([[makeQuery(id+"F14.imprint","IMPRINT",EDGE,{"derivedFrom":subQ7}),1.0]])]});}
            extrude(context, id + "F15", {"entities" : qUnion([Q0]), "operationType" : NewBodyOperationType.REMOVE, "oppositeDirection" : true, "depth" : 3.8 * mm});
        }
        {
            var Q0;
            Q0=makeQuery(id+"F12.opExtrude","CAP_FACE",FACE,{"disambiguationData":[OSD([sQuery(id+"F0.wireOp",EDGE,"E0.bottom"),sQuery(id+"F0.wireOp",EDGE,"E0.top"),sQuery(id+"F0.wireOp",EDGE,"E0.left")])],"isStart":false});
            extrude(context, id + "F16", {"entities" : qUnion([Q0]), "operationType" : NewBodyOperationType.REMOVE, "oppositeDirection" : true, "depth" : 10.16 * mm});
        }
        {
            var Q0;
            Q0=makeQuery(id+"F13.opExtrude","CAP_FACE",FACE,{"disambiguationData":[OSD([sQuery(id+"F0.wireOp",EDGE,"E0.bottom"),sQuery(id+"F0.wireOp",EDGE,"E0.top"),sQuery(id+"F0.wireOp",EDGE,"E0.right")])],"isStart":false});
            extrude(context, id + "F17", {"entities" : qUnion([Q0]), "operationType" : NewBodyOperationType.REMOVE, "oppositeDirection" : true, "depth" : 10.16 * mm});
        }
    });
